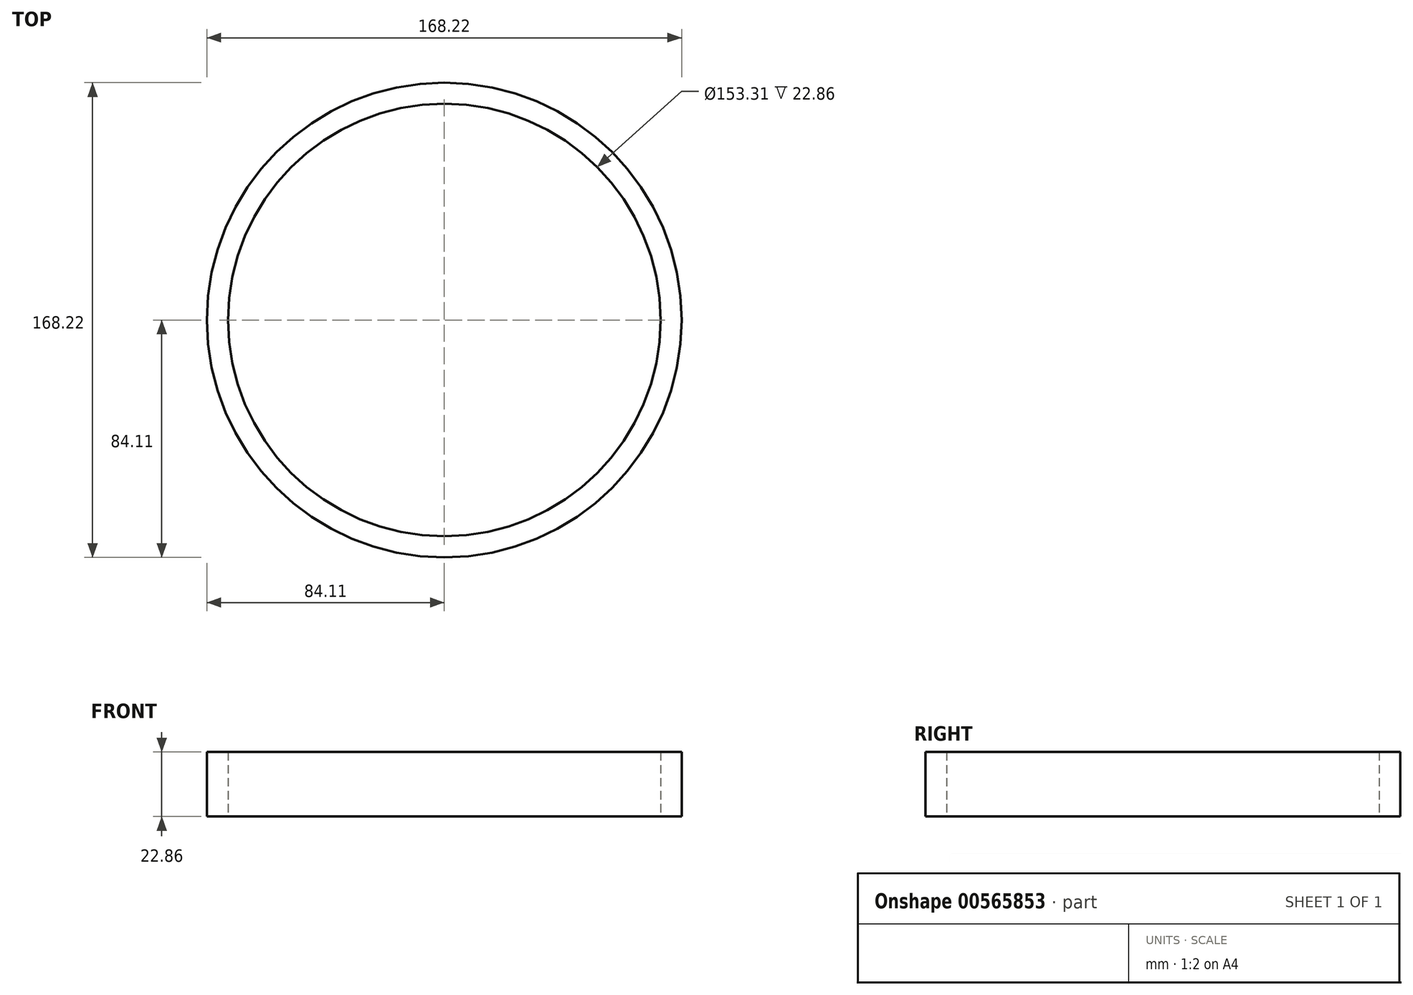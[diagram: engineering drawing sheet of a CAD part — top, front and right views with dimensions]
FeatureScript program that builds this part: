
annotation { "Feature Type Name" : "Feature", "Feature Type Description" : "" }
export const myFeature = defineFeature(function(context is Context, id is Id, definition is map)
    precondition{}
    {
        {
            var Q0;
            Q0=qCreatedBy(makeId("Top.planeOp"),FACE);
            var sketch = newSketch(context, id + "F0", { "sketchPlane" : qUnion([Q0])});
            skCircle(sketch, "E0", {"center": v(0, 0) * mm, "radius": 84.11 * mm});
            skCircle(sketch, "E1", {"center": v(0, 0) * mm, "radius": 76.65 * mm});
            skSolve(sketch);
        }
        {
            var Q0;
            Q0=makeQuery(id+"F0.imprint","IMPRINT",FACE,{"disambiguationData":[TD([[makeQuery(id+"F0.imprint","IMPRINT",EDGE,{"derivedFrom":sQuery(id+"F0.wireOp",EDGE,"E0")}),1.0]])]});
            extrude(context, id + "F1", {"entities" : qUnion([Q0]), "endBound" : BoundingType.SYMMETRIC, "depth" : 22.86 * mm, "offsetDistance" : 25.4 * mm});
        }
    });
